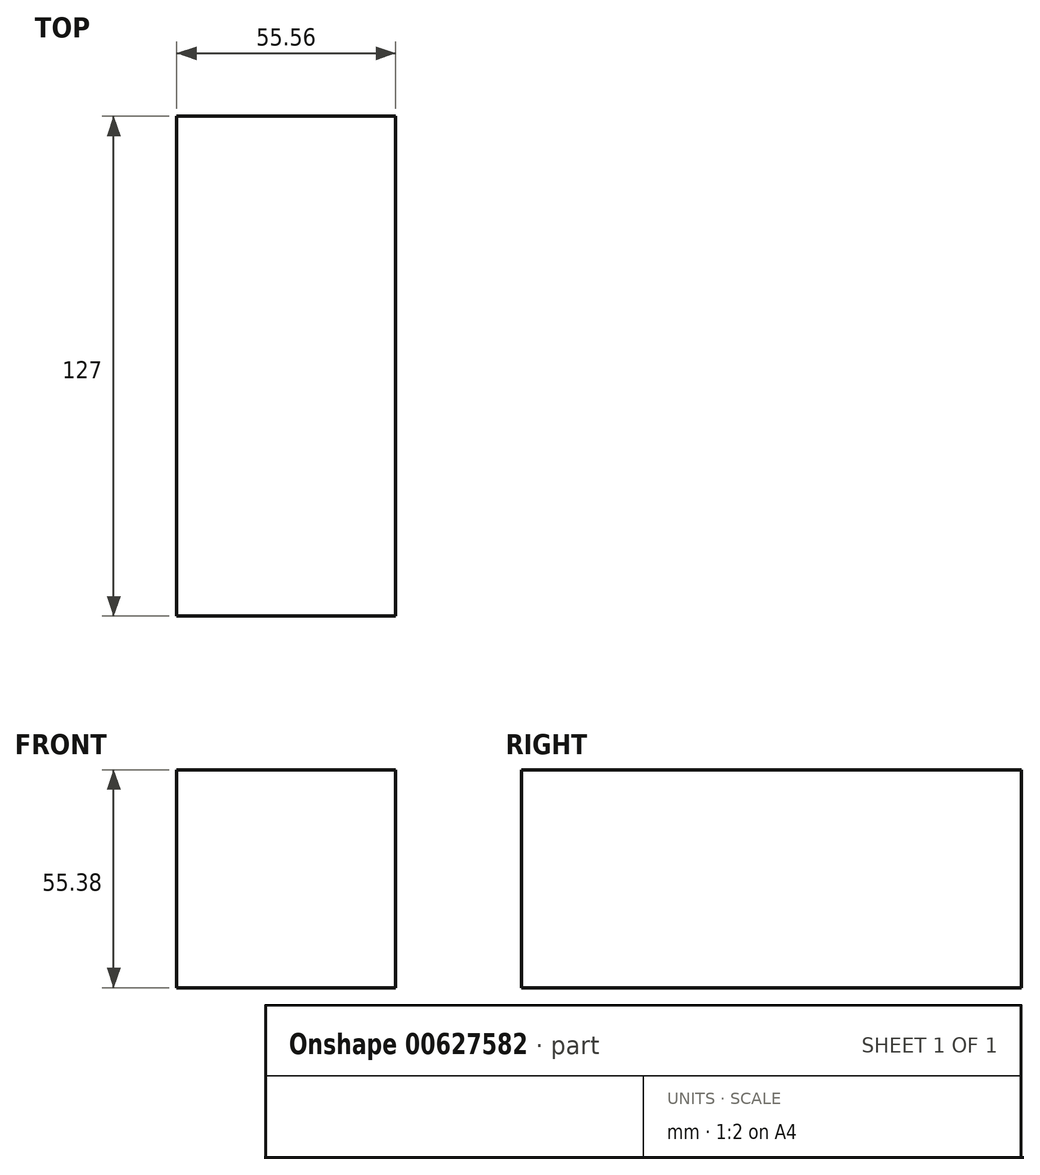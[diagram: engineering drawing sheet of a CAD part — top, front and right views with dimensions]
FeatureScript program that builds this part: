
annotation { "Feature Type Name" : "Feature", "Feature Type Description" : "" }
export const myFeature = defineFeature(function(context is Context, id is Id, definition is map)
    precondition{}
    {
        {
            var Q0;
            Q0=qCreatedBy(makeId("Front.planeOp"),FACE);
            var sketch = newSketch(context, id + "F0", { "sketchPlane" : qUnion([Q0])});
            skLineSegment(sketch, "E0.bottom", {"start": v(-21.67, 36.95) * mm, "end": v(33.9, 36.95) * mm});
            skLineSegment(sketch, "E0.top", {"start": v(-21.67, -18.43) * mm, "end": v(33.9, -18.43) * mm});
            skLineSegment(sketch, "E0.left", {"start": v(-21.67, 36.95) * mm, "end": v(-21.67, -18.43) * mm});
            skLineSegment(sketch, "E0.right", {"start": v(33.9, 36.95) * mm, "end": v(33.9, -18.43) * mm});
            skSolve(sketch);
        }
        {
            var Q0;
            Q0=makeQuery(id+"F0.imprint","IMPRINT",FACE,{"disambiguationData":[TD([[makeQuery(id+"F0.imprint","IMPRINT",EDGE,{"derivedFrom":sQuery(id+"F0.wireOp",EDGE,"E0.bottom")}),-1.0]])]});
            extrude(context, id + "F1", {"entities" : qUnion([Q0]), "depth" : 127 * mm, "offsetDistance" : 25.4 * mm});
        }
    });
